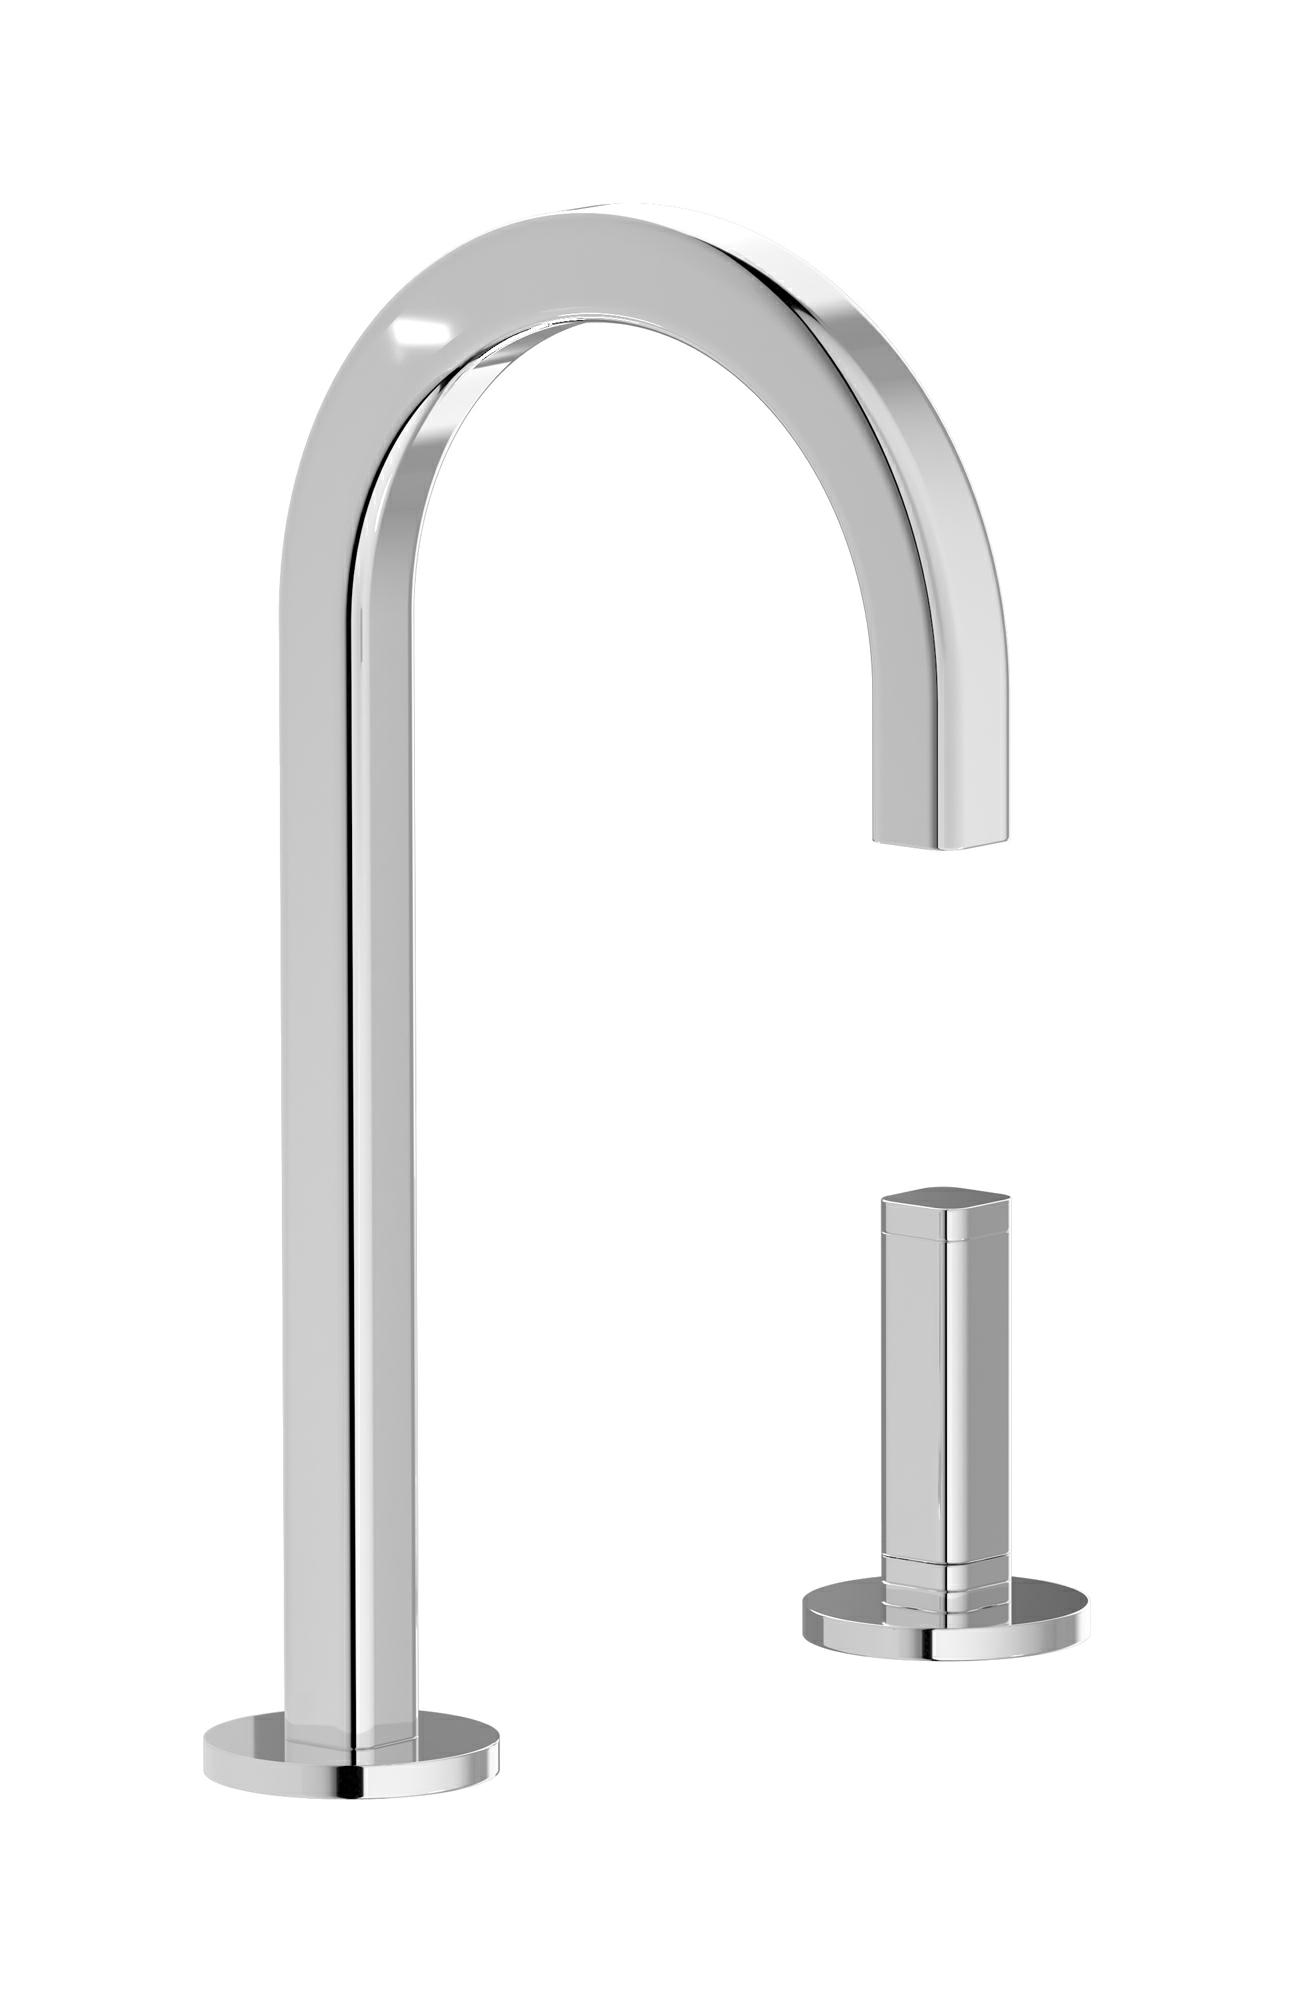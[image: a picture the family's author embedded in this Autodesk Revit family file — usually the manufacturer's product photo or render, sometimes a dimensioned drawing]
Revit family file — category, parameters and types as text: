
# Revit family: EI394_3
name_source: partatom
category: Apparecchi idraulici
units: mm (PartAtom-declared; Revit-internal decimal feet)

## family parameters
Basato su piano di lavoro = No
Condiviso = No
Mantieni orientamento annotazione = No
Numero OmniClass = 23.45.55.17
Punto di calcolo locali = No
Quota connettore circolare = Usa diametro
Sempre verticale = Sì
Taglio con vuoti quando caricato = No
Tipo di parte = Normale
Titolo OmniClass = Mixing Faucets

## types (12) — shared parameters
Cold water flow = 0,0 L/s
Cold water inlet = 10 mm  [stored 0.0328084 ft]
Commenti sul tipo = Washbasin
Connessione CW = No
Connessione HW = No
Connessione di scarico = No
Connessione di ventilazione = No
Descrizione = Washbasin two hole mixer
Hot water inlet = 10 mm  [stored 0.0328084 ft]
Produttore = IB Rubinetterie S.p.A.
URL = https://www.weareib.it
zero-valued in all types: Prospetto di default

## per-type parameters (varying)
| type | Finishes surface | Immagine tipo | Modello |
| Chrome | IB_Chrome | EI394CC_3.jpg | EI394CC_3 |
| Brushed nickel | IB_Brushed nickel | EI394SS_3.jpg | EI394SS_3 |
| Matt black | IB_matt black | EI394NP_3.jpg | EI394NP_3 |
| Natural brass | IB_Brass | EI394ON_3.jpg | EI394ON_3 |
| Black chrome | IB_Black chrome | EI394CF_3.jpg | EI394CF_3 |
| Brushed black chrome | IB_Brushed black chrome | EI394CS_3.jpg | EI394CS_3 |
| Pale gold | IB_Pale gold | EI394II_3.jpg | EI394II_3 |
| Brushed pale gold | IB_brushed pale gold | EI394IS_3.jpg | EI394IS_3 |
| Rose gold | IB_Rose gold | EI394RS_3.jpg | EI394RS_3 |
| Brushed rose gold | IB_Brushed rose gold | EI394SR_3.jpg | EI394SR_3 |
| Gold | IB_gold | EI394OO_3.jpg | EI394OO_3 |
| Brushed gold | IB_gold | EI394OS_3.jpg | EI394OS_3 |

note: [stored X ft] marks values corroborated as IEEE doubles in the binary element streams (Revit-internal decimal feet)
